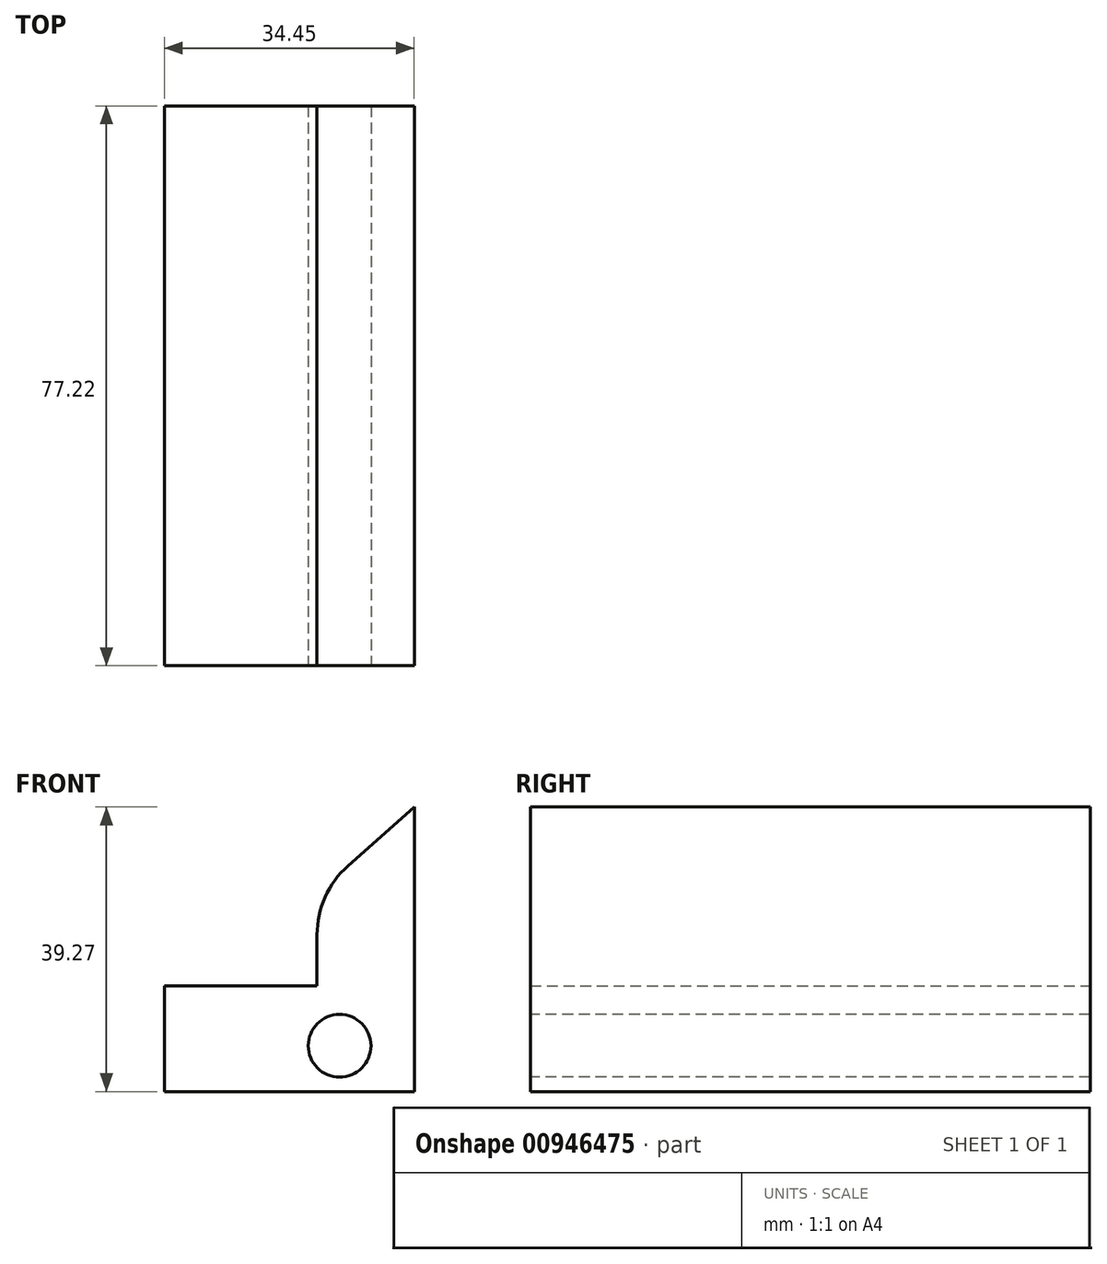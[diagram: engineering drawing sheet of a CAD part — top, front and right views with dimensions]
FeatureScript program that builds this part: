
annotation { "Feature Type Name" : "Feature", "Feature Type Description" : "" }
export const myFeature = defineFeature(function(context is Context, id is Id, definition is map)
    precondition{}
    {
        {
            var Q0;
            Q0=qCreatedBy(makeId("Front.planeOp"),FACE);
            var sketch = newSketch(context, id + "F0", { "sketchPlane" : qUnion([Q0])});
            skLineSegment(sketch, "E0", {"start": v(0, 0) * mm, "end": v(34.45, 0) * mm});
            skLineSegment(sketch, "E1", {"start": v(34.45, 0) * mm, "end": v(34.45, 39.27) * mm});
            skLineSegment(sketch, "E2", {"start": v(34.45, 39.27) * mm, "end": v(21.05, 27.33) * mm});
            skLineSegment(sketch, "E3", {"start": v(21.05, 27.33) * mm, "end": v(21.05, 14.56) * mm});
            skLineSegment(sketch, "E4", {"start": v(21.05, 14.56) * mm, "end": v(0, 14.56) * mm});
            skLineSegment(sketch, "E5", {"start": v(0, 14.56) * mm, "end": v(0, 0) * mm});
            skSolve(sketch);
        }
        {
            var Q0;
            Q0 = qSketchRegion(id + "F0", true);
            extrude(context, id + "F1", {"entities" : qUnion([Q0]), "depth" : 77.22 * mm, "offsetDistance" : 25.4 * mm});
        }
        {
            var Q0;
            Q0=makeQuery(id+"F1.opExtrude","SWEPT_EDGE",EDGE,{"disambiguationData":[OSD([sQuery(id+"F0.wireOp",EDGE,"E2"),sQuery(id+"F0.wireOp",EDGE,"E3")])]});
            fillet(context, id + "F2", {"entities" : qUnion([Q0]), "radius" : 12.7 * mm, "tangentPropagation" : true, "allowEdgeOverflow" : false});
        }
        {
            var Q0;
            Q0=makeQuery(id+"F1.opExtrude","CAP_FACE",FACE,{"disambiguationData":[OSD([sQuery(id+"F0.wireOp",EDGE,"E0"),sQuery(id+"F0.wireOp",EDGE,"E1"),sQuery(id+"F0.wireOp",EDGE,"E2"),sQuery(id+"F0.wireOp",EDGE,"E3"),sQuery(id+"F0.wireOp",EDGE,"E4"),sQuery(id+"F0.wireOp",EDGE,"E5")])],"isStart":false});
            var sketch = newSketch(context, id + "F3", { "sketchPlane" : qUnion([Q0])});
            skCircle(sketch, "E6", {"center": v(24.16, 6.31) * mm, "radius": 4.32 * mm});
            skSolve(sketch);
        }
        {
            var Q0;
            Q0 = qSketchRegion(id + "F3", true);
            var Q1;
            Q1=makeQuery(id+"F1.opExtrude","CAP_FACE",FACE,{"disambiguationData":[OSD([sQuery(id+"F0.wireOp",EDGE,"E0"),sQuery(id+"F0.wireOp",EDGE,"E1"),sQuery(id+"F0.wireOp",EDGE,"E2"),sQuery(id+"F0.wireOp",EDGE,"E3"),sQuery(id+"F0.wireOp",EDGE,"E4"),sQuery(id+"F0.wireOp",EDGE,"E5")])],"isStart":true});
            extrude(context, id + "F4", {"entities" : qUnion([Q0]), "operationType" : NewBodyOperationType.REMOVE, "endBound" : BoundingType.UP_TO_SURFACE, "oppositeDirection" : true, "depth" : 25.4 * mm, "endBoundEntityFace" : qUnion([Q1]), "offsetDistance" : 25.4 * mm});
        }
    });
